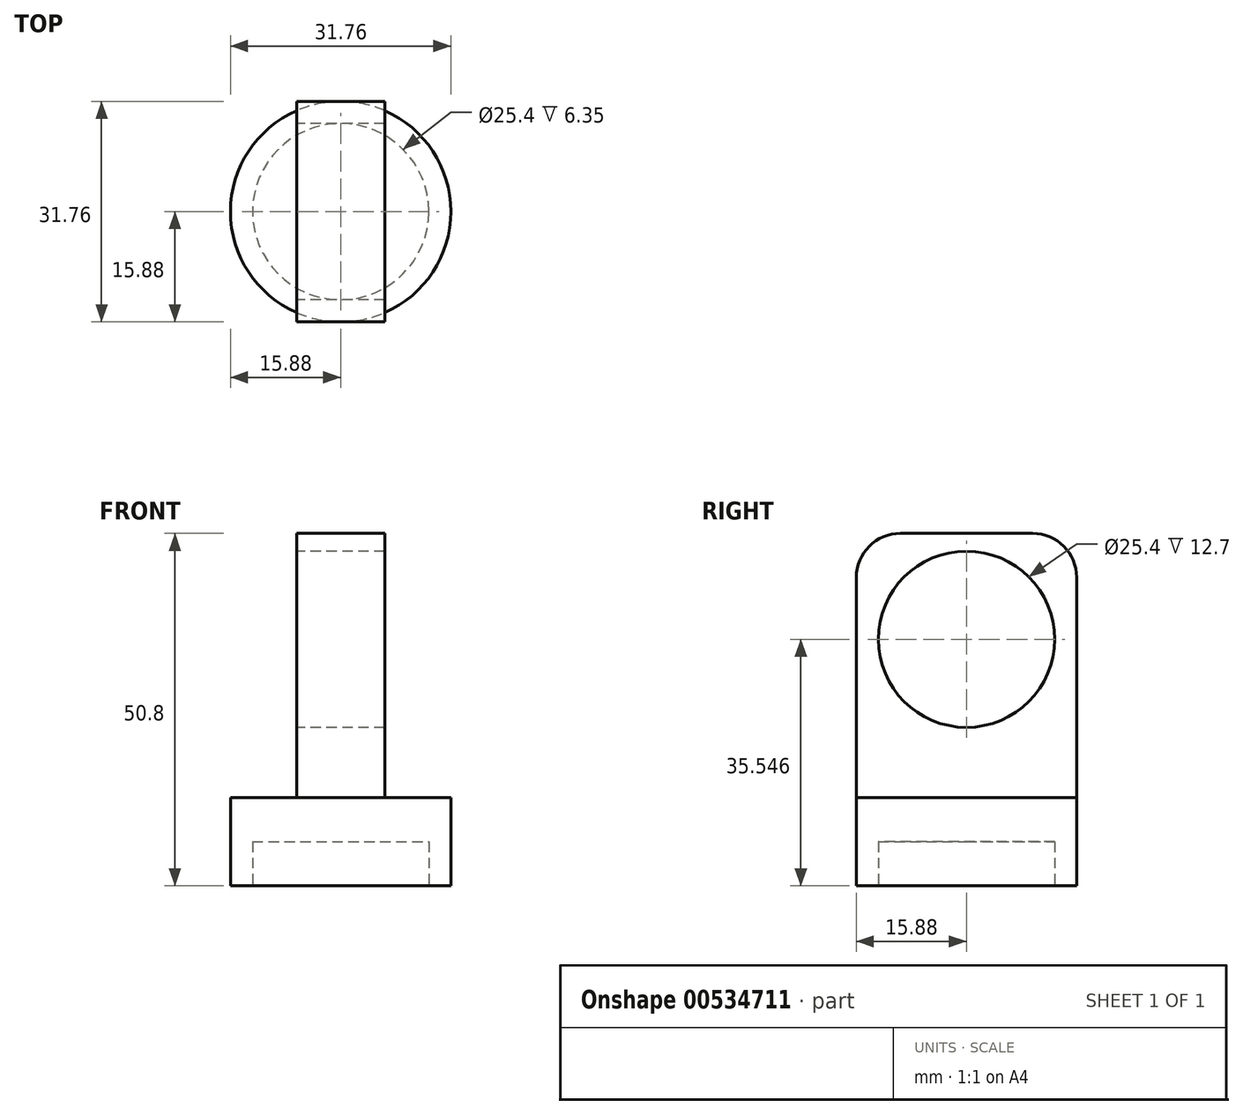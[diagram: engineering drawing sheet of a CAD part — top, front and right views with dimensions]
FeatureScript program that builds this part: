
annotation { "Feature Type Name" : "Feature", "Feature Type Description" : "" }
export const myFeature = defineFeature(function(context is Context, id is Id, definition is map)
    precondition{}
    {
        {
            var Q0;
            Q0=qCreatedBy(makeId("Right.planeOp"),FACE);
            var sketch = newSketch(context, id + "F0", { "sketchPlane" : qUnion([Q0])});
            skLineSegment(sketch, "E0.bottom", {"start": v(15.87, 0) * mm, "end": v(-15.88, 0) * mm});
            skLineSegment(sketch, "E0.top", {"start": v(9.52, 38.1) * mm, "end": v(-9.52, 38.1) * mm});
            skLineSegment(sketch, "E0.left", {"start": v(15.87, 0) * mm, "end": v(15.87, 31.75) * mm});
            skLineSegment(sketch, "E0.right", {"start": v(-15.88, 0) * mm, "end": v(-15.88, 31.75) * mm});
            skPoint(sketch, "E0.middle", {"position": v(0, 19.05) * mm});
            skLineSegment(sketch, "E1", {"start": v(0, 66.54) * mm, "end": v(0, -15.42) * mm, "construction": true});
            skCircle(sketch, "E2", {"center": v(0, 22.85) * mm, "radius": 12.7 * mm});
            skPoint(sketch, "E3.visualSharp", {"position": v(15.87, 38.1) * mm});
            skArc(sketch, "E3.filletArc", {"start": v(15.87, 31.75) * mm, "mid": v(14.02, 36.24) * mm, "end": v(9.52, 38.1) * mm});
            skPoint(sketch, "E4.visualSharp", {"position": v(-15.88, 38.1) * mm});
            skArc(sketch, "E4.filletArc", {"start": v(-9.52, 38.1) * mm, "mid": v(-14.02, 36.24) * mm, "end": v(-15.88, 31.75) * mm});
            skSolve(sketch);
        }
        {
            var Q0;
            Q0=qCreatedBy(makeId("Top.planeOp"),FACE);
            var sketch = newSketch(context, id + "F1", { "sketchPlane" : qUnion([Q0])});
            skCircle(sketch, "E5", {"center": v(0, 0) * mm, "radius": 15.88 * mm});
            skCircle(sketch, "E6", {"center": v(0, 0) * mm, "radius": 12.7 * mm});
            skSolve(sketch);
        }
        {
            var Q0;
            Q0=makeQuery(id+"F0.imprint","IMPRINT",FACE,{"disambiguationData":[TD([[makeQuery(id+"F0.imprint","IMPRINT",EDGE,{"derivedFrom":sQuery(id+"F0.wireOp",EDGE,"E0.bottom")}),-1.0]])]});
            extrude(context, id + "F2", {"entities" : qUnion([Q0]), "depth" : 6.35 * mm, "offsetDistance" : 25.4 * mm});
        }
        {
            var Q0;
            Q0=makeQuery(id+"F2.opExtrude","CAP_FACE",FACE,{"disambiguationData":[OSD([sQuery(id+"F0.wireOp",EDGE,"E0.bottom"),sQuery(id+"F0.wireOp",EDGE,"E0.top"),sQuery(id+"F0.wireOp",EDGE,"E0.left"),sQuery(id+"F0.wireOp",EDGE,"E0.right"),sQuery(id+"F0.wireOp",EDGE,"E2"),sQuery(id+"F0.wireOp",EDGE,"E3.filletArc"),sQuery(id+"F0.wireOp",EDGE,"E4.filletArc")])],"isStart":true});
            extrude(context, id + "F3", {"entities" : qUnion([Q0]), "operationType" : NewBodyOperationType.ADD, "depth" : 6.35 * mm, "offsetDistance" : 25.4 * mm});
        }
        {
            var Q0;
            Q0=makeQuery(id+"F1.imprint","IMPRINT",FACE,{"disambiguationData":[TD([[makeQuery(id+"F1.imprint","IMPRINT",EDGE,{"derivedFrom":sQuery(id+"F1.wireOp",EDGE,"E6")}),1.0]])]});
            var Q1;
            Q1=makeQuery(id+"F1.imprint","IMPRINT",FACE,{"disambiguationData":[TD([[makeQuery(id+"F1.imprint","IMPRINT",EDGE,{"derivedFrom":sQuery(id+"F1.wireOp",EDGE,"E5")}),1.0]])]});
            extrude(context, id + "F4", {"entities" : qUnion([Q0, Q1]), "operationType" : NewBodyOperationType.ADD, "oppositeDirection" : true, "depth" : 12.7 * mm, "offsetDistance" : 25.4 * mm});
        }
        {
            var Q0;
            Q0=makeQuery(id+"F4.opExtrude","CAP_FACE",FACE,{"disambiguationData":[OSD([sQuery(id+"F1.wireOp",EDGE,"E5")])],"isStart":false});
            var sketch = newSketch(context, id + "F5", { "sketchPlane" : qUnion([Q0])});
            skCircle(sketch, "E7", {"center": v(0, 0) * mm, "radius": 12.7 * mm});
            skSolve(sketch);
        }
        {
            var Q0;
            Q0=makeQuery(id+"F5.imprint","IMPRINT",FACE,{"disambiguationData":[TD([[makeQuery(id+"F5.imprint","IMPRINT",EDGE,{"derivedFrom":sQuery(id+"F5.wireOp",EDGE,"E7")}),1.0]])]});
            extrude(context, id + "F6", {"entities" : qUnion([Q0]), "operationType" : NewBodyOperationType.REMOVE, "oppositeDirection" : true, "depth" : 6.35 * mm, "offsetDistance" : 25.4 * mm});
        }
    });
